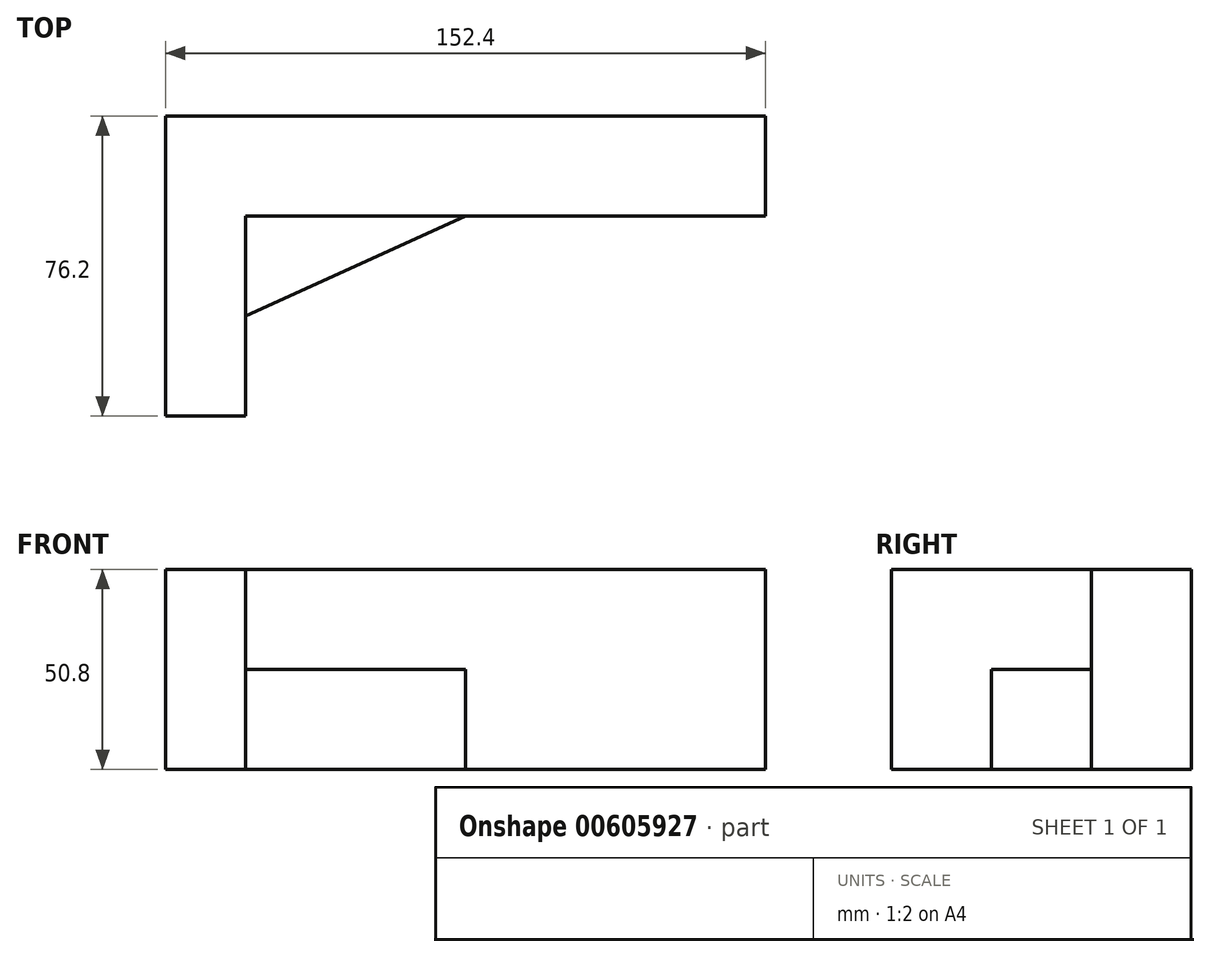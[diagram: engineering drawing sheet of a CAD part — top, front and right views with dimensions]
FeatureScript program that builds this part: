
annotation { "Feature Type Name" : "Feature", "Feature Type Description" : "" }
export const myFeature = defineFeature(function(context is Context, id is Id, definition is map)
    precondition{}
    {
        {
            var Q0;
            Q0=qCreatedBy(makeId("Top.planeOp"),FACE);
            var sketch = newSketch(context, id + "F0", { "sketchPlane" : qUnion([Q0])});
            skLineSegment(sketch, "E0", {"start": v(0, 0) * mm, "end": v(0, 76.2) * mm});
            skLineSegment(sketch, "E1", {"start": v(0, 76.2) * mm, "end": v(152.4, 76.2) * mm});
            skLineSegment(sketch, "E2", {"start": v(152.4, 76.2) * mm, "end": v(152.4, 50.8) * mm});
            skLineSegment(sketch, "E3", {"start": v(152.4, 50.8) * mm, "end": v(76.2, 50.8) * mm});
            skLineSegment(sketch, "E4", {"start": v(-5.11, 0) * mm, "end": v(20.29, 0) * mm});
            skLineSegment(sketch, "E5", {"start": v(20.29, 0) * mm, "end": v(20.29, 25.4) * mm});
            skLineSegment(sketch, "E6", {"start": v(20.29, 25.4) * mm, "end": v(76.2, 50.8) * mm});
            skLineSegment(sketch, "E7", {"start": v(76.2, 50.8) * mm, "end": v(20.29, 50.8) * mm});
            skLineSegment(sketch, "E8", {"start": v(20.29, 50.8) * mm, "end": v(20.29, 25.4) * mm});
            skSolve(sketch);
        }
        {
            var Q0;
            {var subQ0=sQuery(id+"F0.wireOp",EDGE,"E0");Q0=makeQuery(id+"F0.imprint","IMPRINT",FACE,{"disambiguationData":[TD([[makeQuery(id+"F0.imprint","IMPRINT",EDGE,{"derivedFrom":subQ0}),-1.0]])]});}
            var Q1;
            Q1=makeQuery(id+"F0.imprint","IMPRINT",FACE,{"disambiguationData":[TD([[makeQuery(id+"F0.imprint","IMPRINT",EDGE,{"derivedFrom":sQuery(id+"F0.wireOp",EDGE,"E6")}),1.0]])]});
            extrude(context, id + "F1", {"entities" : qUnion([Q0, Q1]), "depth" : 50.8 * mm, "offsetDistance" : 25.4 * mm});
        }
        {
            var Q0;
            Q0=makeQuery(id+"F1.opExtrude","CAP_FACE",FACE,{"disambiguationData":[OSD([sQuery(id+"F0.wireOp",EDGE,"E0"),sQuery(id+"F0.wireOp",EDGE,"E1"),sQuery(id+"F0.wireOp",EDGE,"E2"),sQuery(id+"F0.wireOp",EDGE,"E3"),sQuery(id+"F0.wireOp",EDGE,"E4"),sQuery(id+"F0.wireOp",EDGE,"E5"),sQuery(id+"F0.wireOp",EDGE,"E6")])],"isStart":false});
            var sketch = newSketch(context, id + "F2", { "sketchPlane" : qUnion([Q0])});
            skLineSegment(sketch, "E9", {"start": v(20.29, 25.4) * mm, "end": v(20.29, 50.8) * mm});
            skLineSegment(sketch, "E10", {"start": v(20.29, 50.8) * mm, "end": v(76.2, 50.8) * mm});
            skSolve(sketch);
        }
        {
            var Q0;
            Q0=makeQuery(id+"F2.imprint","IMPRINT",FACE,{"disambiguationData":[TD([[makeQuery(id+"F2.imprint","IMPRINT",EDGE,{"derivedFrom":sQuery(id+"F2.wireOp",EDGE,"E9")}),-1.0]])]});
            extrude(context, id + "F3", {"entities" : qUnion([Q0]), "operationType" : NewBodyOperationType.REMOVE, "oppositeDirection" : true, "depth" : 25.4 * mm, "offsetDistance" : 25.4 * mm});
        }
    });
